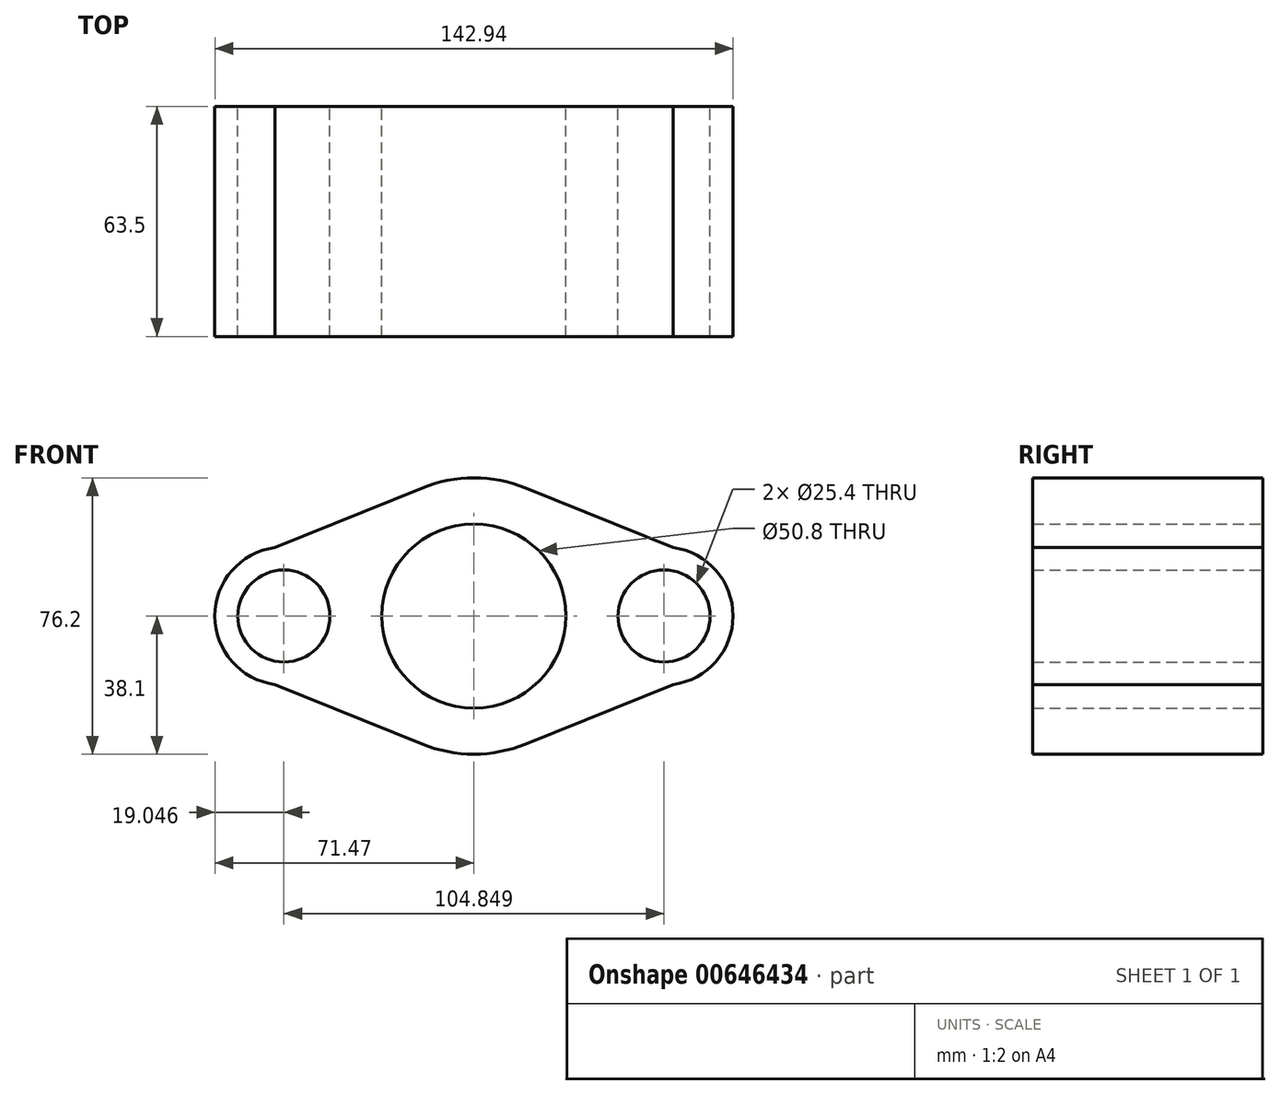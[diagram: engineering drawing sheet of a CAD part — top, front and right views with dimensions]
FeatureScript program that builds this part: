
annotation { "Feature Type Name" : "Feature", "Feature Type Description" : "" }
export const myFeature = defineFeature(function(context is Context, id is Id, definition is map)
    precondition{}
    {
        {
            var Q0;
            Q0=qCreatedBy(makeId("Front.planeOp"),FACE);
            var sketch = newSketch(context, id + "F0", { "sketchPlane" : qUnion([Q0])});
            skArc(sketch, "E0", {"start": v(-14.28, -35.32) * mm, "mid": v(0, -38.1) * mm, "end": v(14.28, -35.32) * mm});
            skCircle(sketch, "E1", {"center": v(0, 0) * mm, "radius": 25.4 * mm});
            skCircle(sketch, "E2", {"center": v(-52.42, 0) * mm, "radius": 12.7 * mm});
            skArc(sketch, "E3", {"start": v(-54.95, 18.88) * mm, "mid": v(-71.47, 0) * mm, "end": v(-54.95, -18.88) * mm});
            skLineSegment(sketch, "E4", {"start": v(-54.95, 18.88) * mm, "end": v(-14.28, 35.32) * mm});
            skArc(sketch, "E5.MirrorC", {"start": v(54.95, 18.88) * mm, "mid": v(71.47, 0) * mm, "end": v(54.95, -18.88) * mm});
            skCircle(sketch, "E6.MirrorC", {"center": v(52.42, 0) * mm, "radius": 12.7 * mm});
            skLineSegment(sketch, "E7.MirrorCS", {"start": v(54.95, 18.88) * mm, "end": v(14.28, 35.32) * mm});
            skLineSegment(sketch, "E8.MirrorCS", {"start": v(-54.95, -18.88) * mm, "end": v(-14.28, -35.32) * mm});
            skLineSegment(sketch, "E9.MirrorCS", {"start": v(54.95, -18.88) * mm, "end": v(14.28, -35.32) * mm});
            skArc(sketch, "E10.trimOffspring", {"start": v(14.28, 35.32) * mm, "mid": v(0, 38.1) * mm, "end": v(-14.28, 35.32) * mm});
            skSolve(sketch);
        }
        {
            var Q0;
            Q0 = qSketchRegion(id + "F0", true);
            extrude(context, id + "F1", {"entities" : qUnion([Q0]), "depth" : 63.5 * mm, "offsetDistance" : 25.4 * mm});
        }
    });
